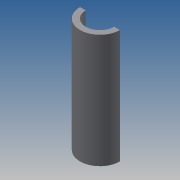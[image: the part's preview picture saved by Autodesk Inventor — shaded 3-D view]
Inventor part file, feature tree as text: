
AUTODESK INVENTOR PART (.ipt)
format: ipt  version: 2014 SP1 (Build 180222100, 222)  size: 70,656 bytes
history: native  units: in
note: dims shown in document units (in); Inventor stores cm internally (conversion verified against a paired STEP export)
features: extrude x1, sketch x1
ambient origin geometry x8: Origin, YZ Plane, XZ Plane, XY Plane, X Axis, Y Axis, Z Axis, Center Point
bodies: Solid1 (feature_tree)
feature tree (2):
  extrude  "Extrusion1"  Depth=2.0in
  sketch  "Sketch1"  dims[d0=0.7in d1=0.1in d2=2.0in d3=0.0in]
